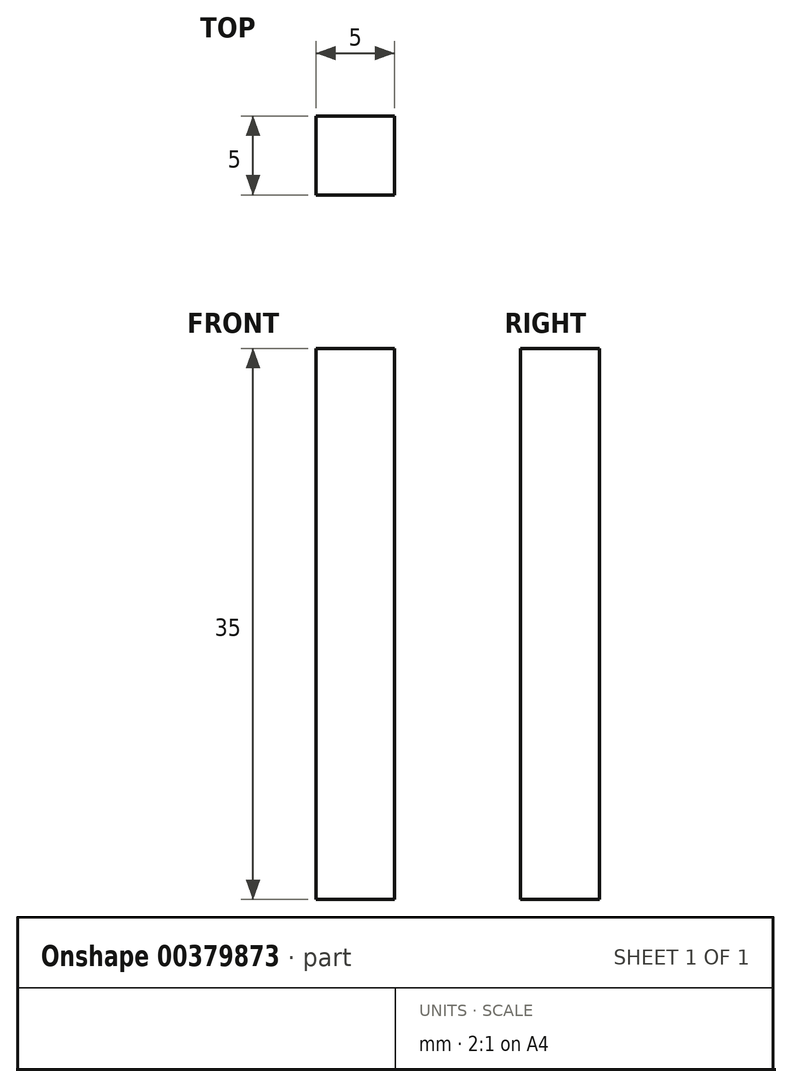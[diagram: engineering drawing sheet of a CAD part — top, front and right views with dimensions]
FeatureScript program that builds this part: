
annotation { "Feature Type Name" : "Feature", "Feature Type Description" : "" }
export const myFeature = defineFeature(function(context is Context, id is Id, definition is map)
    precondition{}
    {
        {
            var Q0;
            Q0=qCreatedBy(makeId("Front.planeOp"),FACE);
            var sketch = newSketch(context, id + "F0", { "sketchPlane" : qUnion([Q0])});
            skLineSegment(sketch, "E0.bottom", {"start": v(0, 0) * mm, "end": v(5, 0) * mm});
            skLineSegment(sketch, "E0.top", {"start": v(0, 35) * mm, "end": v(5, 35) * mm});
            skLineSegment(sketch, "E0.left", {"start": v(0, 0) * mm, "end": v(0, 35) * mm});
            skLineSegment(sketch, "E0.right", {"start": v(5, 0) * mm, "end": v(5, 35) * mm});
            skSolve(sketch);
        }
        {
            var Q0;
            Q0=makeQuery(id+"F0.imprint","IMPRINT",FACE,{"disambiguationData":[TD([[makeQuery(id+"F0.imprint","IMPRINT",EDGE,{"derivedFrom":sQuery(id+"F0.wireOp",EDGE,"E0.bottom")}),1.0]])]});
            extrude(context, id + "F1", {"entities" : qUnion([Q0]), "depth" : 5 * mm});
        }
    });
